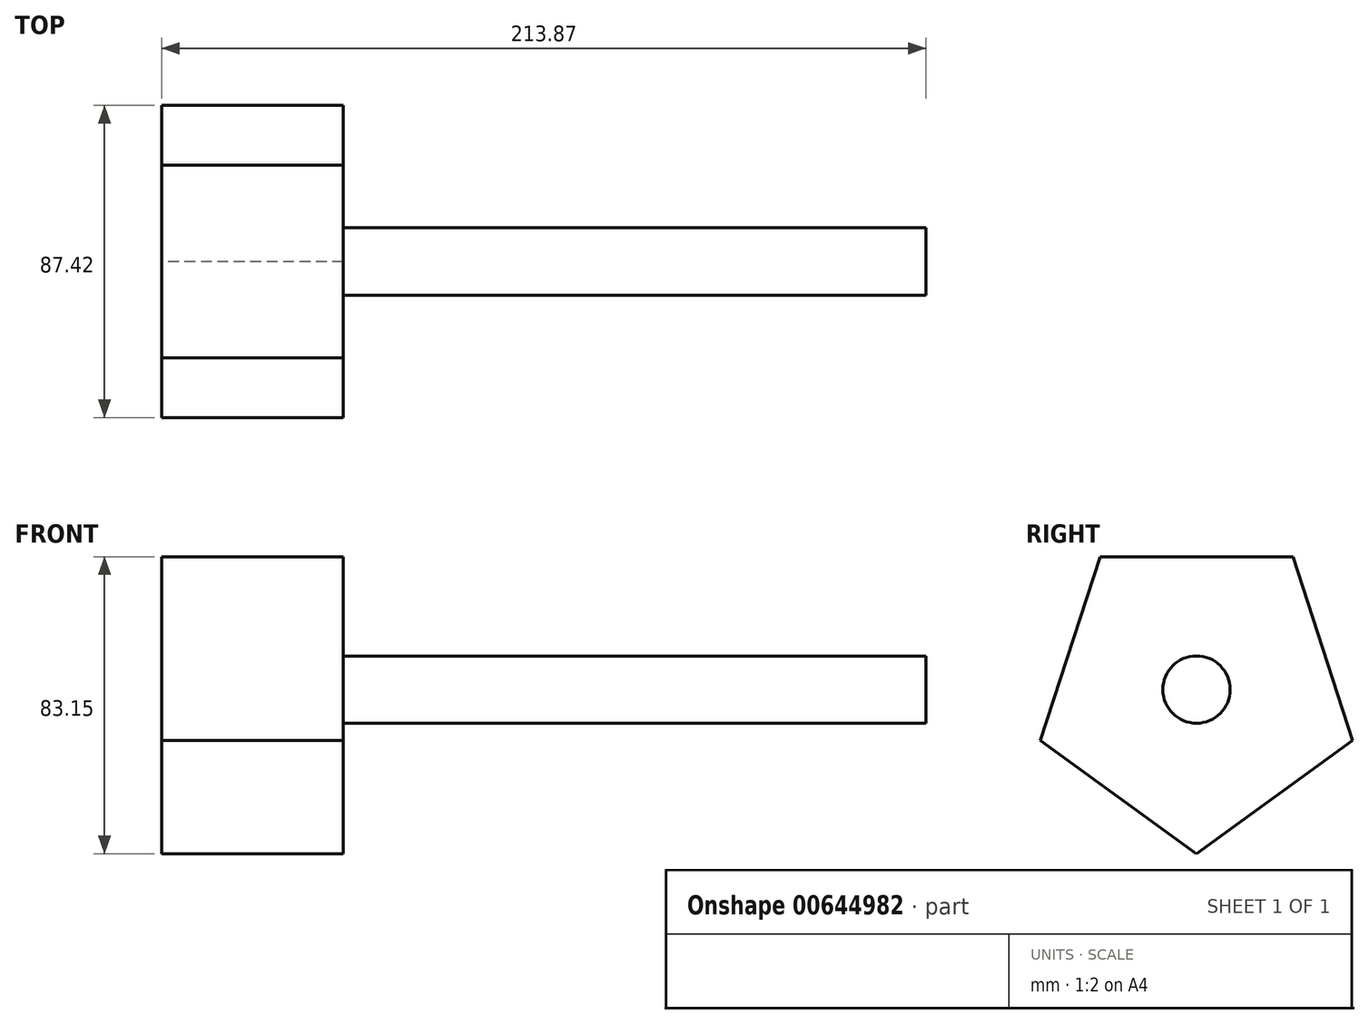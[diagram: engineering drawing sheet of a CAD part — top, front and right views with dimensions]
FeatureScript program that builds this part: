
annotation { "Feature Type Name" : "Feature", "Feature Type Description" : "" }
export const myFeature = defineFeature(function(context is Context, id is Id, definition is map)
    precondition{}
    {
        {
            var Q0;
            Q0=qCreatedBy(makeId("Right.planeOp"),FACE);
            var sketch = newSketch(context, id + "F0", { "sketchPlane" : qUnion([Q0])});
            skCircle(sketch, "E0", {"center": v(0, 0) * mm, "radius": 9.43 * mm});
            skSolve(sketch);
        }
        {
            var Q0;
            Q0 = qSketchRegion(id + "F0", true);
            extrude(context, id + "F1", {"entities" : qUnion([Q0]), "depth" : 213.87 * mm, "offsetDistance" : 25.4 * mm});
        }
        {
            var Q0;
            Q0=makeQuery(id+"F1.opExtrude","CAP_FACE",FACE,{"disambiguationData":[OSD([sQuery(id+"F0.wireOp",EDGE,"E0")])],"isStart":true});
            var sketch = newSketch(context, id + "F2", { "sketchPlane" : qUnion([Q0])});
            skCircle(sketch, "E1.cCircle", {"center": v(0, 0) * mm, "radius": 37.19 * mm, "construction": true});
            skLineSegment(sketch, "E1.0", {"start": v(-27.02, 37.19) * mm, "end": v(27.02, 37.19) * mm});
            skLineSegment(sketch, "E1.1", {"start": v(27.02, 37.19) * mm, "end": v(43.71, -14.2) * mm});
            skLineSegment(sketch, "E1.2", {"start": v(43.71, -14.2) * mm, "end": v(0, -45.96) * mm});
            skLineSegment(sketch, "E1.3", {"start": v(0, -45.96) * mm, "end": v(-43.71, -14.2) * mm});
            skLineSegment(sketch, "E1.4", {"start": v(-43.71, -14.2) * mm, "end": v(-27.02, 37.19) * mm});
            skPoint(sketch, "E1.0.midPoint", {"position": v(0, 37.19) * mm});
            skSolve(sketch);
        }
        {
            var Q0;
            Q0 = qSketchRegion(id + "F2", true);
            extrude(context, id + "F3", {"entities" : qUnion([Q0]), "operationType" : NewBodyOperationType.ADD, "oppositeDirection" : true, "depth" : 50.8 * mm, "offsetDistance" : 25.4 * mm});
        }
    });
